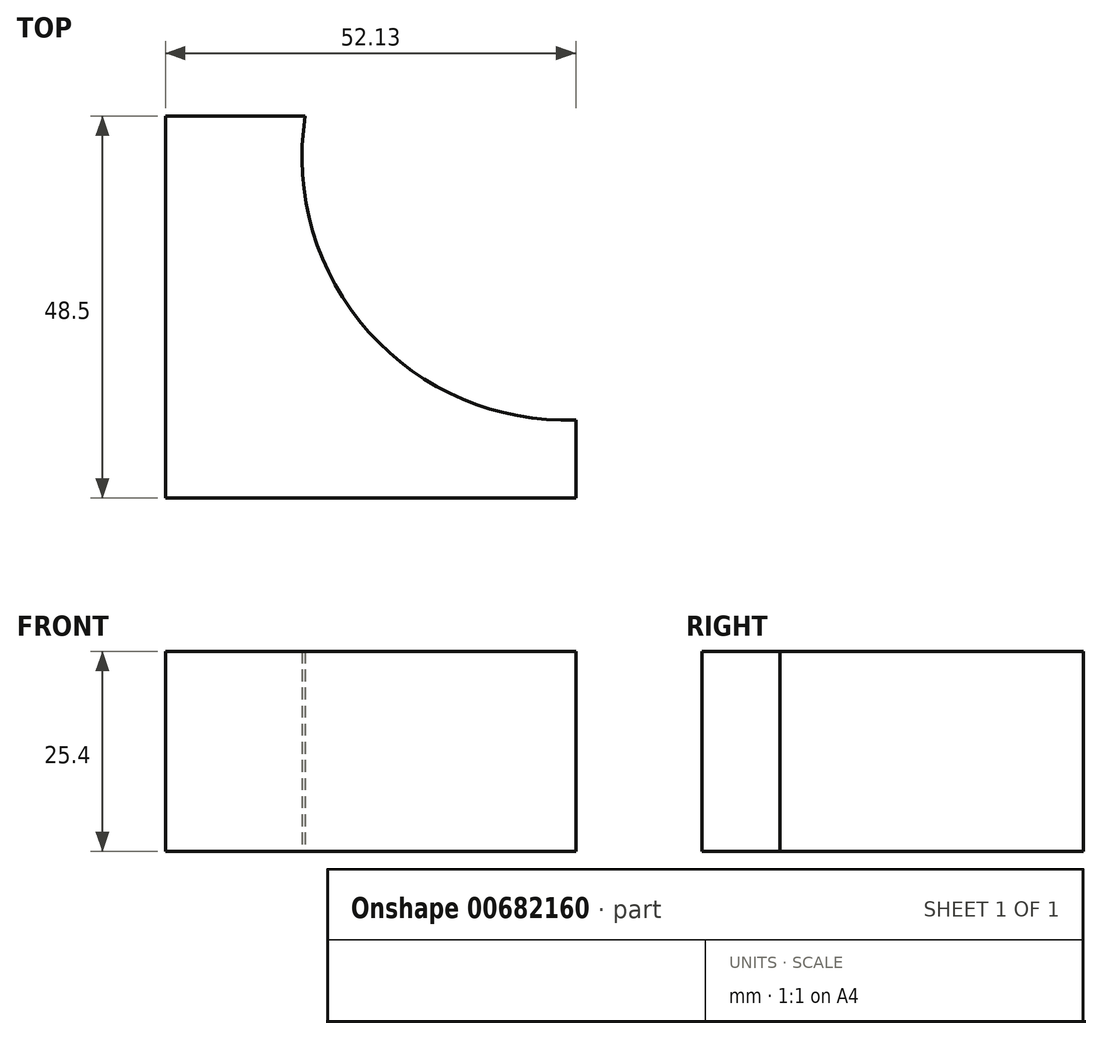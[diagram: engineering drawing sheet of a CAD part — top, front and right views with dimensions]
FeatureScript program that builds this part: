
annotation { "Feature Type Name" : "Feature", "Feature Type Description" : "" }
export const myFeature = defineFeature(function(context is Context, id is Id, definition is map)
    precondition{}
    {
        {
            var Q0;
            Q0=qCreatedBy(makeId("Top.planeOp"),FACE);
            var sketch = newSketch(context, id + "F0", { "sketchPlane" : qUnion([Q0])});
            skLineSegment(sketch, "E0", {"start": v(-22.82, 41.53) * mm, "end": v(-40.58, 41.53) * mm});
            skLineSegment(sketch, "E1", {"start": v(-40.58, 41.53) * mm, "end": v(-40.58, -6.97) * mm});
            skLineSegment(sketch, "E2", {"start": v(-40.58, -6.97) * mm, "end": v(11.55, -6.97) * mm});
            skLineSegment(sketch, "E3", {"start": v(11.55, -6.97) * mm, "end": v(11.55, 2.96) * mm});
            skArc(sketch, "E4", {"start": v(-22.82, 41.53) * mm, "mid": v(-14.75, 14.12) * mm, "end": v(11.55, 2.96) * mm});
            skSolve(sketch);
        }
        {
            var Q0;
            Q0 = qSketchRegion(id + "F0", true);
            extrude(context, id + "F1", {"entities" : qUnion([Q0]), "depth" : 25.4 * mm, "offsetDistance" : 25.4 * mm});
        }
    });
